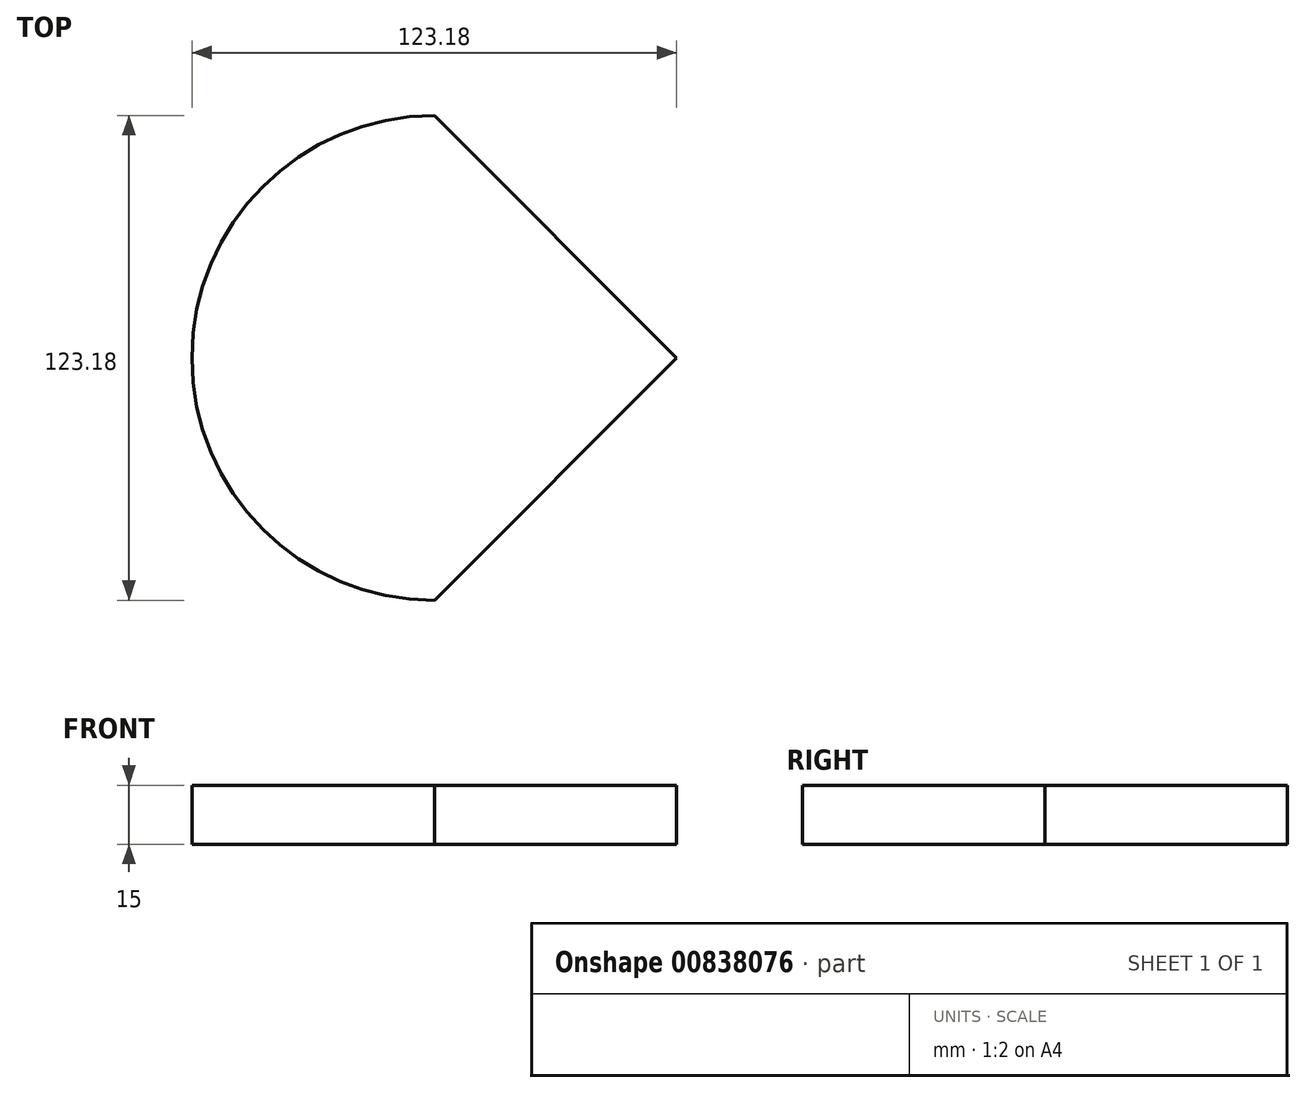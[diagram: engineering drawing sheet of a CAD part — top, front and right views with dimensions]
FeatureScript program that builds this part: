
annotation { "Feature Type Name" : "Feature", "Feature Type Description" : "" }
export const myFeature = defineFeature(function(context is Context, id is Id, definition is map)
    precondition{}
    {
        {
            var Q0;
            Q0=qCreatedBy(makeId("Top.planeOp"),FACE);
            var sketch = newSketch(context, id + "F0", { "sketchPlane" : qUnion([Q0])});
            skArc(sketch, "E0", {"start": v(0, 61.59) * mm, "mid": v(-61.59, 0) * mm, "end": v(0, -61.59) * mm});
            skLineSegment(sketch, "E1", {"start": v(0, 61.59) * mm, "end": v(61.59, 0) * mm});
            skLineSegment(sketch, "E2", {"start": v(61.59, 0) * mm, "end": v(0, -61.59) * mm});
            skLineSegment(sketch, "E3", {"start": v(0, 0) * mm, "end": v(0, -61.59) * mm});
            skLineSegment(sketch, "E4", {"start": v(0, 0) * mm, "end": v(0, 81.27) * mm, "construction": true});
            skSolve(sketch);
        }
        {
            var Q0;
            Q0 = qSketchRegion(id + "F0", true);
            extrude(context, id + "F1", {"entities" : qUnion([Q0]), "depth" : 15 * mm, "offsetDistance" : 25 * mm});
        }
    });
